# Revit family: Luna 10
name_source: partatom
category: Generic Models
revit_build: Autodesk Revit 2018 (Build: 20180423_1000(x64)
units: mm (PartAtom-declared; Revit-internal decimal feet)

## family parameters
Always vertical = Yes
Can host rebar = No
Cut with Voids When Loaded = No
Part Type = Normal
Room Calculation Point = No
Round Connector Dimension = Use Diameter
Shared = No
Work Plane-Based = No

## types (2) — shared parameters
Breedte = 329 mm  [stored 1.0794 ft]
Colour = Kunststof buitenkant
Diepte = 239 mm
Hoogte = 450 mm  [stored 1.47638 ft]
Logo = MW logo
Manufacturer = Masterwatt B.V.
Phase = 1
URL = https://masterwatt.nl
Voltage = 230 V

## per-type parameters (varying)
| type | Power (default) |
| Luna 10 | 2000 VA |
| Luna 10 Hotfill | 600 VA |

note: column(s) folded — value = type name in every type: Model

note: [stored X ft] marks values corroborated as IEEE doubles in the binary element streams (Revit-internal decimal feet)

## geometry (parser evidence)
native form markers: Sweep x7
no freeform markers — native parametric forms only
